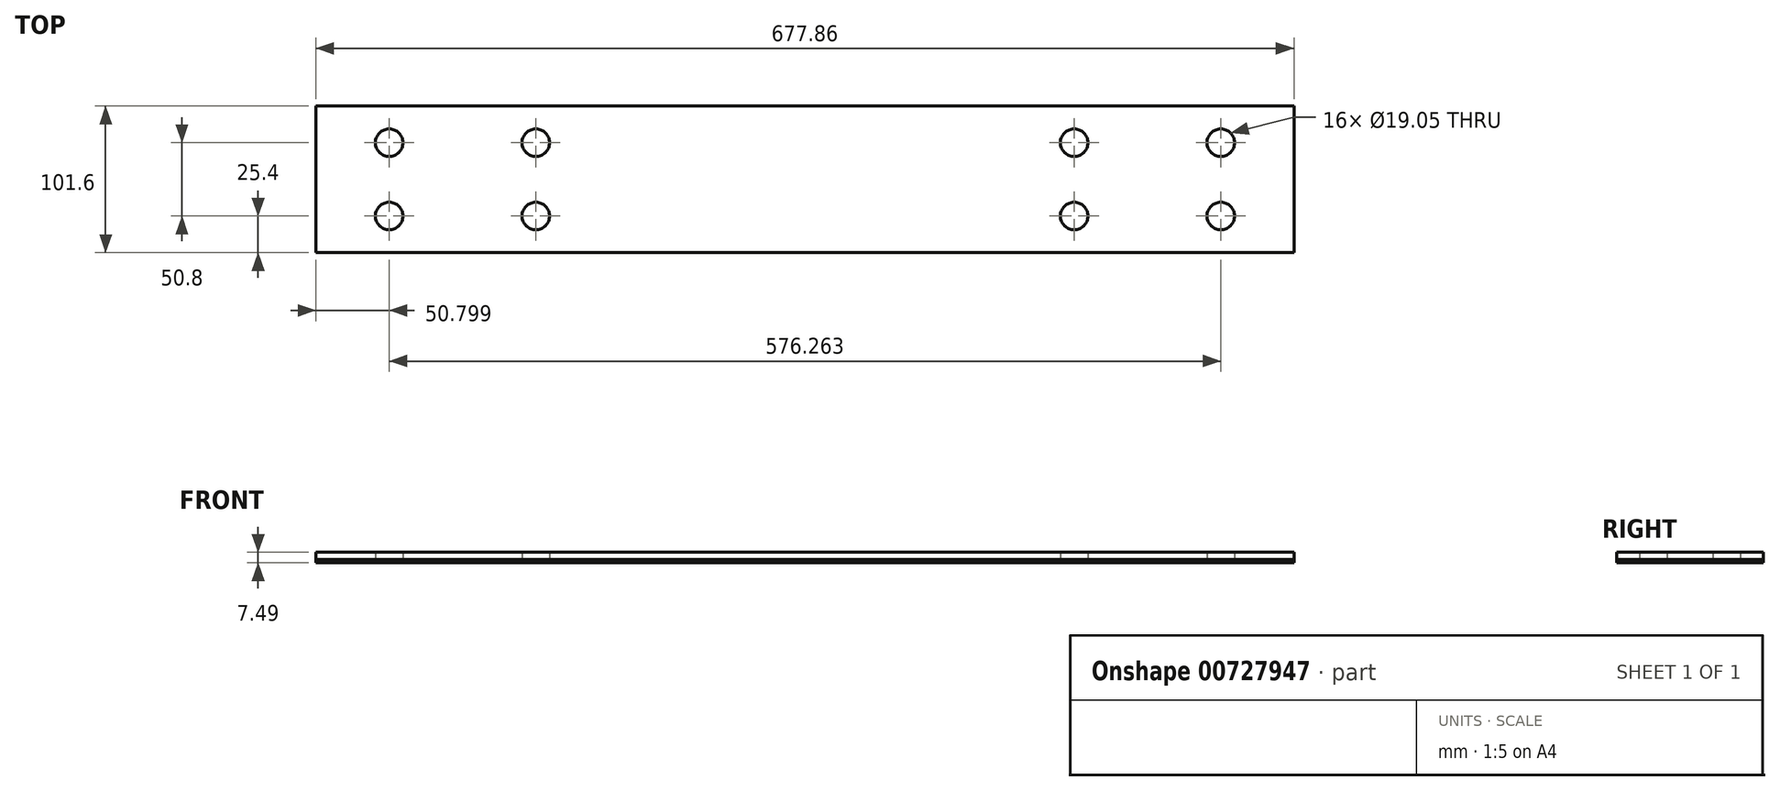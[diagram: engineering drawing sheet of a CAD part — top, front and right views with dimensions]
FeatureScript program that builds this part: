
annotation { "Feature Type Name" : "Feature", "Feature Type Description" : "" }
export const myFeature = defineFeature(function(context is Context, id is Id, definition is map)
    precondition{}
    {
        {
            var Q0;
            Q0=qCreatedBy(makeId("Top.planeOp"),FACE);
            var sketch = newSketch(context, id + "F0", { "sketchPlane" : qUnion([Q0])});
            skLineSegment(sketch, "E0.bottom", {"start": v(338.93, -50.8) * mm, "end": v(-338.93, -50.8) * mm});
            skLineSegment(sketch, "E0.top", {"start": v(338.93, 50.8) * mm, "end": v(-338.93, 50.8) * mm});
            skLineSegment(sketch, "E0.left", {"start": v(338.93, -50.8) * mm, "end": v(338.93, 50.8) * mm});
            skLineSegment(sketch, "E0.right", {"start": v(-338.93, -50.8) * mm, "end": v(-338.93, 50.8) * mm});
            skPoint(sketch, "E0.middle", {"position": v(0, 0) * mm});
            skCircle(sketch, "E1", {"center": v(-288.13, 25.4) * mm, "radius": 9.53 * mm});
            skCircle(sketch, "E2", {"center": v(-186.53, 25.4) * mm, "radius": 9.53 * mm});
            skCircle(sketch, "E3", {"center": v(-288.13, -25.4) * mm, "radius": 9.53 * mm});
            skCircle(sketch, "E4.MirrorC", {"center": v(-186.53, -25.4) * mm, "radius": 9.53 * mm});
            skCircle(sketch, "E5.MirrorC", {"center": v(186.53, 25.4) * mm, "radius": 9.53 * mm});
            skCircle(sketch, "E6.MirrorC", {"center": v(186.53, -25.4) * mm, "radius": 9.53 * mm});
            skCircle(sketch, "E7.MirrorC", {"center": v(288.13, 25.4) * mm, "radius": 9.53 * mm});
            skCircle(sketch, "E8.MirrorC", {"center": v(288.13, -25.4) * mm, "radius": 9.53 * mm});
            skSolve(sketch);
        }
        {
            var Q0;
            Q0 = qSketchRegion(id + "F0", true);
            extrude(context, id + "F1", {"entities" : qUnion([Q0]), "depth" : 5.08 * mm, "offsetDistance" : 25.4 * mm});
        }
        {
            var Q0;
            Q0=makeQuery(id+"F1.opExtrude","CAP_FACE",FACE,{"disambiguationData":[OSD([sQuery(id+"F0.wireOp",EDGE,"E0.bottom"),sQuery(id+"F0.wireOp",EDGE,"E0.top"),sQuery(id+"F0.wireOp",EDGE,"E0.left"),sQuery(id+"F0.wireOp",EDGE,"E0.right"),sQuery(id+"F0.wireOp",EDGE,"E1"),sQuery(id+"F0.wireOp",EDGE,"E2"),sQuery(id+"F0.wireOp",EDGE,"E3"),sQuery(id+"F0.wireOp",EDGE,"E4.MirrorC"),sQuery(id+"F0.wireOp",EDGE,"E5.MirrorC"),sQuery(id+"F0.wireOp",EDGE,"E6.MirrorC"),sQuery(id+"F0.wireOp",EDGE,"E7.MirrorC"),sQuery(id+"F0.wireOp",EDGE,"E8.MirrorC")])],"isStart":true});
            var sketch = newSketch(context, id + "F2", { "sketchPlane" : qUnion([Q0])});
            skLineSegment(sketch, "E9.bottom", {"start": v(-338.93, 50.8) * mm, "end": v(338.93, 50.8) * mm});
            skLineSegment(sketch, "E9.top", {"start": v(-338.93, -50.8) * mm, "end": v(338.93, -50.8) * mm});
            skLineSegment(sketch, "E9.left", {"start": v(-338.93, 50.8) * mm, "end": v(-338.93, -50.8) * mm});
            skLineSegment(sketch, "E9.right", {"start": v(338.93, 50.8) * mm, "end": v(338.93, -50.8) * mm});
            skCircle(sketch, "E10", {"center": v(-288.13, 25.4) * mm, "radius": 9.53 * mm});
            skCircle(sketch, "E11", {"center": v(-186.53, 25.4) * mm, "radius": 9.53 * mm});
            skCircle(sketch, "E12.MirrorC", {"center": v(-186.53, -25.4) * mm, "radius": 9.53 * mm});
            skCircle(sketch, "E13.MirrorC", {"center": v(-288.13, -25.4) * mm, "radius": 9.53 * mm});
            skCircle(sketch, "E14.MirrorC", {"center": v(186.53, 25.4) * mm, "radius": 9.53 * mm});
            skCircle(sketch, "E15.MirrorC", {"center": v(186.53, -25.4) * mm, "radius": 9.53 * mm});
            skCircle(sketch, "E16.MirrorC", {"center": v(288.13, 25.4) * mm, "radius": 9.53 * mm});
            skCircle(sketch, "E17.MirrorC", {"center": v(288.13, -25.4) * mm, "radius": 9.53 * mm});
            skSolve(sketch);
        }
        {
            var Q0;
            Q0 = qSketchRegion(id + "F2", true);
            extrude(context, id + "F3", {"entities" : qUnion([Q0]), "depth" : 2.41 * mm, "offsetDistance" : 25.4 * mm});
        }
    });
